# Revit family: Faucet-Cold_Lavatory-KOHLER-Fore-K-30093T
name_source: partatom
category: Plumbing Fixtures
units: mm (PartAtom-declared; Revit-internal decimal feet)

## family parameters
Cut with Voids When Loaded = No
Host = Face
Maintain Annotation Orientation = No
OmniClass Number = 23.31.11.00
OmniClass Title = Faucets
Part Type = Normal
Room Calculation Point = No
Round Connector Dimension = Use Diameter
Shared = No

## types (3) — shared parameters
ADA Compliant = No
Assembly Code = D2010
CW Connection = Yes
Cold Water Inlet = Cold Water Inlet
Date Modified = 03/27/2025
Default Elevation = 36"
Description = Cold Water Lavatory Faucet
Drain Included = No
Flow Rate = 2 GPM
HW Connection = No
Handle Clearance = 3 3/4"
Height = 6"
Hot Water Inlet = Hot Water Inlet
Length = 4 1/2"
Manufacturer = Kohler Co.
Master Format 2014 = 22 41 39
Master Format 2014 Name = Residential Faucets, Supplies, and Trim
Material = Premium Metal Construction
Pressure = 80.00 psi
Product Name = Fore
Spout Reach = 4 1/2"
URL = http://www.kohler.com.cn
Vent Connection = No
Waste Connection = No
Waste Water Outlet = Waste Water Outlet
WaterSense Certified = No
Width = 2"

## per-type parameters (varying)
| type | Finish | Model | Plug Finish | Type |
| AF-Vibrant French Gold | Kohler-Metal-AF-Vibrant_French_Gold | K-30093T-4CD-AF | Silicone-Pantone-Black_C | 1 |
| BL-Matte Black | Kohler-Metal-BL-Matte_Black | K-30093T-4CD-BL | Silicone-Pantone-Black_C | 2 |
| CP-Polished Chrome | Kohler-Metal-CP-Polished_Chrome | K-30093T-4CD-CP | Silicone-Pantone-423C | 3 |

## geometry (parser evidence)
native form markers: Sweep x4
no freeform markers — native parametric forms only
